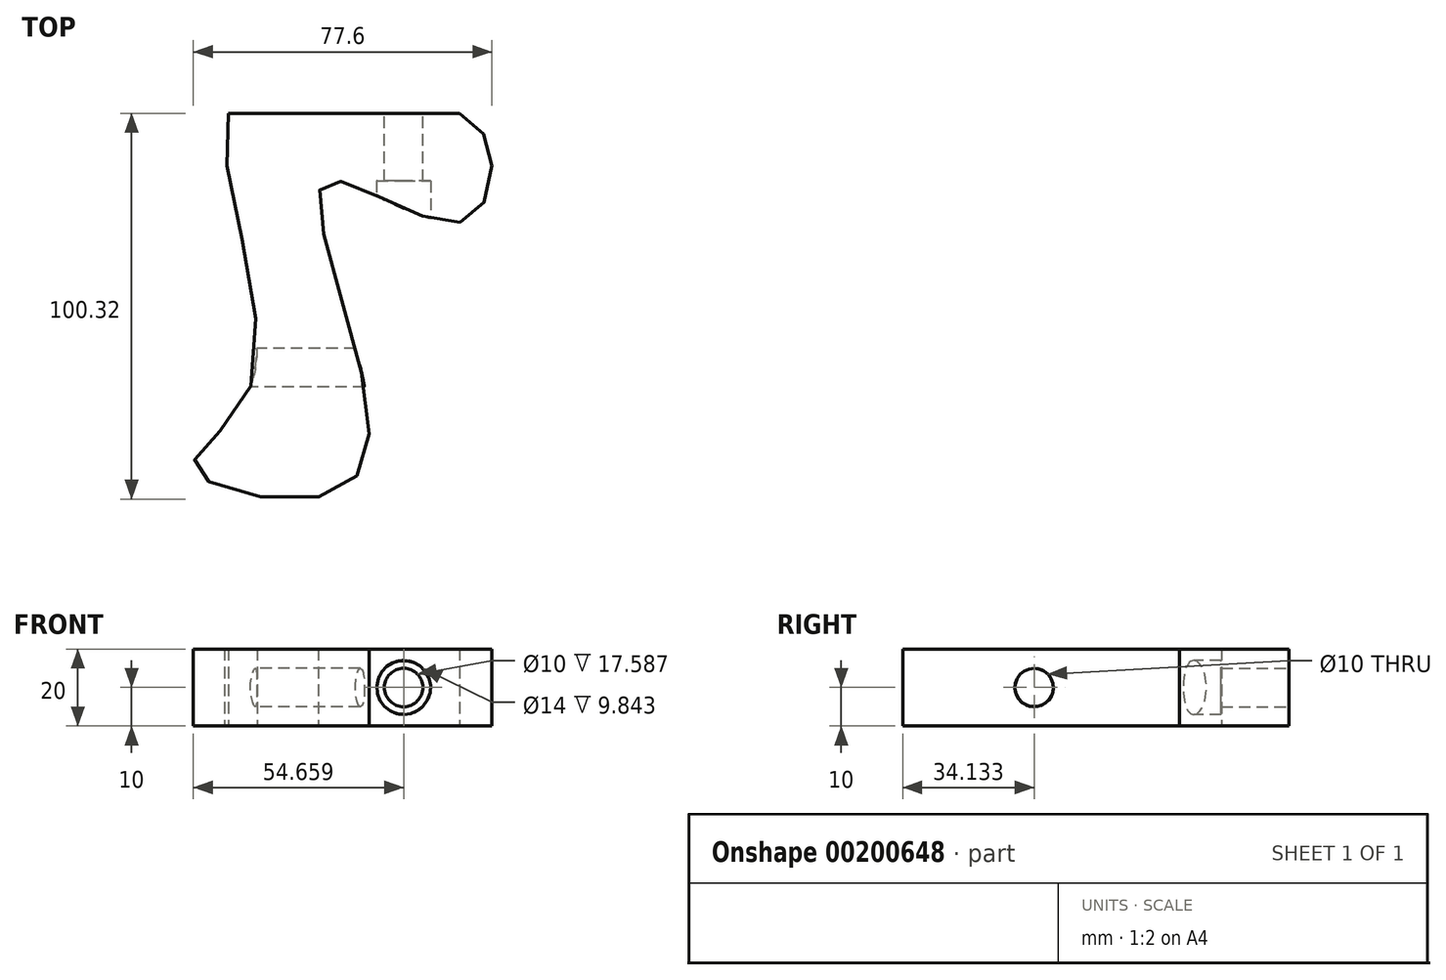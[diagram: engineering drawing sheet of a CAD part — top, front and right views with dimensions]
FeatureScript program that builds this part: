
annotation { "Feature Type Name" : "Feature", "Feature Type Description" : "" }
export const myFeature = defineFeature(function(context is Context, id is Id, definition is map)
    precondition{}
    {
        {
            var Q0;
            Q0=qCreatedBy(makeId("Top.planeOp"),FACE);
            var sketch = newSketch(context, id + "F0", { "sketchPlane" : qUnion([Q0])});
            skFitSpline(sketch, "E0", {"points": [v(17.4, 46.77) * mm, v(-10.85, 42.59) * mm, v(-4.78, -27.45) * mm, v(-19.85, -49.8) * mm, v(14.88, -56.65) * mm, v(24.94, -31.18) * mm, v(13.2, 23.58) * mm, v(28.13, 20.94) * mm, v(51.47, 15) * mm, v(57.45, 31.1) * mm, v(49.15, 42.59) * mm, v(17.4, 46.77) * mm]});
            skLineSegment(sketch, "E1", {"start": v(-10.85, 42.59) * mm, "end": v(49.15, 42.59) * mm});
            skPoint(sketch, "E2", {"position": v(0, -57.41) * mm});
            skSolve(sketch);
        }
        {
            var Q0;
            {var subQ0=sQuery(id+"F0.wireOp",EDGE,"E1");Q0=makeQuery(id+"F0.imprint","IMPRINT",FACE,{"disambiguationData":[TD([[makeQuery(id+"F0.imprint","IMPRINT",EDGE,{"derivedFrom":subQ0}),-1.0]])]});}
            extrude(context, id + "F1", {"entities" : qUnion([Q0]), "depth" : 20 * mm});
        }
        {
            var Q0;
            Q0=makeQuery(id+"F1.opExtrude","SWEPT_FACE",FACE,{"disambiguationData":[OSD([sQuery(id+"F0.wireOp",EDGE,"E1")])]});
            var sketch = newSketch(context, id + "F2", { "sketchPlane" : qUnion([Q0])});
            skLineSegment(sketch, "E3.0.0", {"start": v(-49.15, 0) * mm, "end": v(10.85, 0) * mm});
            skLineSegment(sketch, "E3.0.1", {"start": v(10.85, 0) * mm, "end": v(10.85, 20) * mm});
            skLineSegment(sketch, "E3.0.2", {"start": v(10.85, 20) * mm, "end": v(-49.15, 20) * mm});
            skLineSegment(sketch, "E3.0.3", {"start": v(-49.15, 20) * mm, "end": v(-49.15, 0) * mm});
            skCircle(sketch, "E4", {"center": v(-34.65, 10) * mm, "radius": 5 * mm});
            skPoint(sketch, "E4.centerSnap0", {"position": v(-49.15, 10) * mm});
            skSolve(sketch);
        }
        {
            var Q0;
            Q0=makeQuery(id+"F2.imprint","IMPRINT",FACE,{"disambiguationData":[TD([[makeQuery(id+"F2.imprint","IMPRINT",EDGE,{"derivedFrom":sQuery(id+"F2.wireOp",EDGE,"E4")}),1.0]])]});
            extrude(context, id + "F3", {"entities" : qUnion([Q0]), "operationType" : NewBodyOperationType.REMOVE, "oppositeDirection" : true, "depth" : 30 * mm});
        }
        {
            var Q0;
            Q0=qCreatedBy(makeId("Front.planeOp"),FACE);
            var sketch = newSketch(context, id + "F4", { "sketchPlane" : qUnion([Q0])});
            skCircle(sketch, "E5.0", {"center": v(34.65, 10) * mm, "radius": 5 * mm});
            skCircle(sketch, "E6.0", {"center": v(34.65, 10) * mm, "radius": 7 * mm});
            skSolve(sketch);
        }
        {
            var Q0;
            Q0=makeQuery(id+"F4.imprint","IMPRINT",FACE,{"disambiguationData":[TD([[makeQuery(id+"F4.imprint","IMPRINT",EDGE,{"derivedFrom":sQuery(id+"F4.wireOp",EDGE,"E5.0")}),-1.0]])]});
            extrude(context, id + "F5", {"entities" : qUnion([Q0]), "operationType" : NewBodyOperationType.REMOVE, "oppositeDirection" : true, "depth" : 25 * mm});
        }
        {
            var Q0;
            Q0=qCreatedBy(makeId("Right.planeOp"),FACE);
            cPlane(context, id + "F6", {"entities" : qUnion([Q0]), "cplaneType" : CPlaneType.OFFSET, "offset" : 25 * mm, "oppositeDirection" : true, "width" : 150 * mm, "height" : 150 * mm});
        }
        {
            var Q0;
            Q0=qCreatedBy(id+"F6.planeOp",FACE);
            var sketch = newSketch(context, id + "F7", { "sketchPlane" : qUnion([Q0])});
            skLineSegment(sketch, "E7.0.0", {"start": v(-57.73, 0) * mm, "end": v(25.09, 0) * mm});
            skLineSegment(sketch, "E7.0.1", {"start": v(42.59, 0) * mm, "end": v(42.59, 20) * mm});
            skLineSegment(sketch, "E7.0.2", {"start": v(25.09, 20) * mm, "end": v(-57.73, 20) * mm});
            skLineSegment(sketch, "E7.0.3", {"start": v(42.59, 20) * mm, "end": v(42.59, 0) * mm});
            skCircle(sketch, "E8", {"center": v(-23.6, 10) * mm, "radius": 5 * mm});
            skPoint(sketch, "E8.centerSnap0", {"position": v(42.59, 10) * mm});
            skSolve(sketch);
        }
        {
            var Q0;
            Q0=makeQuery(id+"F7.imprint","IMPRINT",FACE,{"disambiguationData":[TD([[makeQuery(id+"F7.imprint","IMPRINT",EDGE,{"derivedFrom":sQuery(id+"F7.wireOp",EDGE,"E8")}),1.0]])]});
            extrude(context, id + "F8", {"entities" : qUnion([Q0]), "operationType" : NewBodyOperationType.REMOVE, "depth" : 70 * mm});
        }
        {
            var Q0;
            Q0=makeQuery(id+"F1.opExtrude","CAP_FACE",FACE,{"disambiguationData":[OSD([sQuery(id+"F0.wireOp",EDGE,"E0"),sQuery(id+"F0.wireOp",EDGE,"E1")])],"isStart":false});
            extrude(context, id + "F9", {"entities" : qUnion([Q0]), "depth" : 25 * mm});
        }
        {
            var Q0;
            Q0=makeQuery(id+"F9.opExtrude","SWEPT_BODY",BODY,{"disambiguationData":[OSD([sQuery(id+"F0.wireOp",EDGE,"E0"),sQuery(id+"F0.wireOp",EDGE,"E1")])]});
            deleteBodies(context, id + "F10", {"entities" : qUnion([Q0])});
        }
    });
